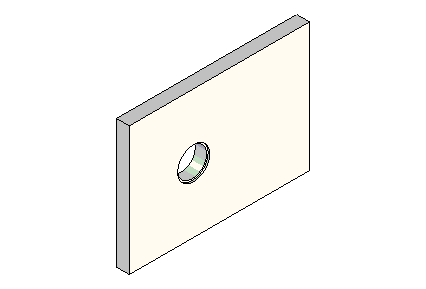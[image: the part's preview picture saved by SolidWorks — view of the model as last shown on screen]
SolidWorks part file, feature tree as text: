
SOLIDWORKS PART (.sldprt)
format: sldprt  version: not decoded by parser v0  size: 222,720 bytes
history: native  units: mm
features: sketch x5, thread x4, cut_extrude x2, extrude x1, hole x1 (+11 scaffold rows collapsed)
feature tree (24):
  scaffold x11  (default folders/planes/origin — collapsed)
  sketch  "Sketch1"  dims[D1=177.8mm D2=127.0mm]
  extrude  "Extrude1"  Depth=12.7mm
  hole  "5/16-18 Tapped Hole1"  Diameter=6.5278mm Depth=22.9235mm
  sketch  "Sketch3"  dims[c1.D1=19.05mm c1.D2=38.1mm c1.D3=38.1mm c1.D4=38.1mm c2.D1=31.75mm]
  sketch  "Sketch2"  dims[hole-wizard template sketch: 47 standard entries collapsed; hole parameters kept: c15.Tap Drill Depth=22.9235mm c15.D3=~14.816244mm c15.Drill Angle=118.0deg]
  thread  "Cosmetic Thread1"  Diameter=15.875mm  [1 undecoded]
  thread  "Cosmetic Thread2"  Diameter=15.875mm  [1 undecoded]
  thread  "Cosmetic Thread3"  Diameter=15.875mm  [1 undecoded]
  thread  "Cosmetic Thread4"  Diameter=15.875mm  [1 undecoded]
  sketch  "Sketch4"  dims[c1.D1=28.575mm c1.D2=28.575mm c1.D3=28.575mm c2.D2=63.5mm c2.D3=63.5mm]
  cut_extrude  "Cut-Extrude1"  [1 undecoded]
  sketch  "Sketch5"  dims[D1=31.75mm]
  cut_extrude  "Cut-Extrude2"  Depth=1.5875mm
decode coverage: 12 of 13 modeling features carry decoded parameters
note: ~ marks probable driven/reference dimensions
note: 5 parameter values undecoded
note: suppression state not decoded; provenance and decode notes live in map.json
